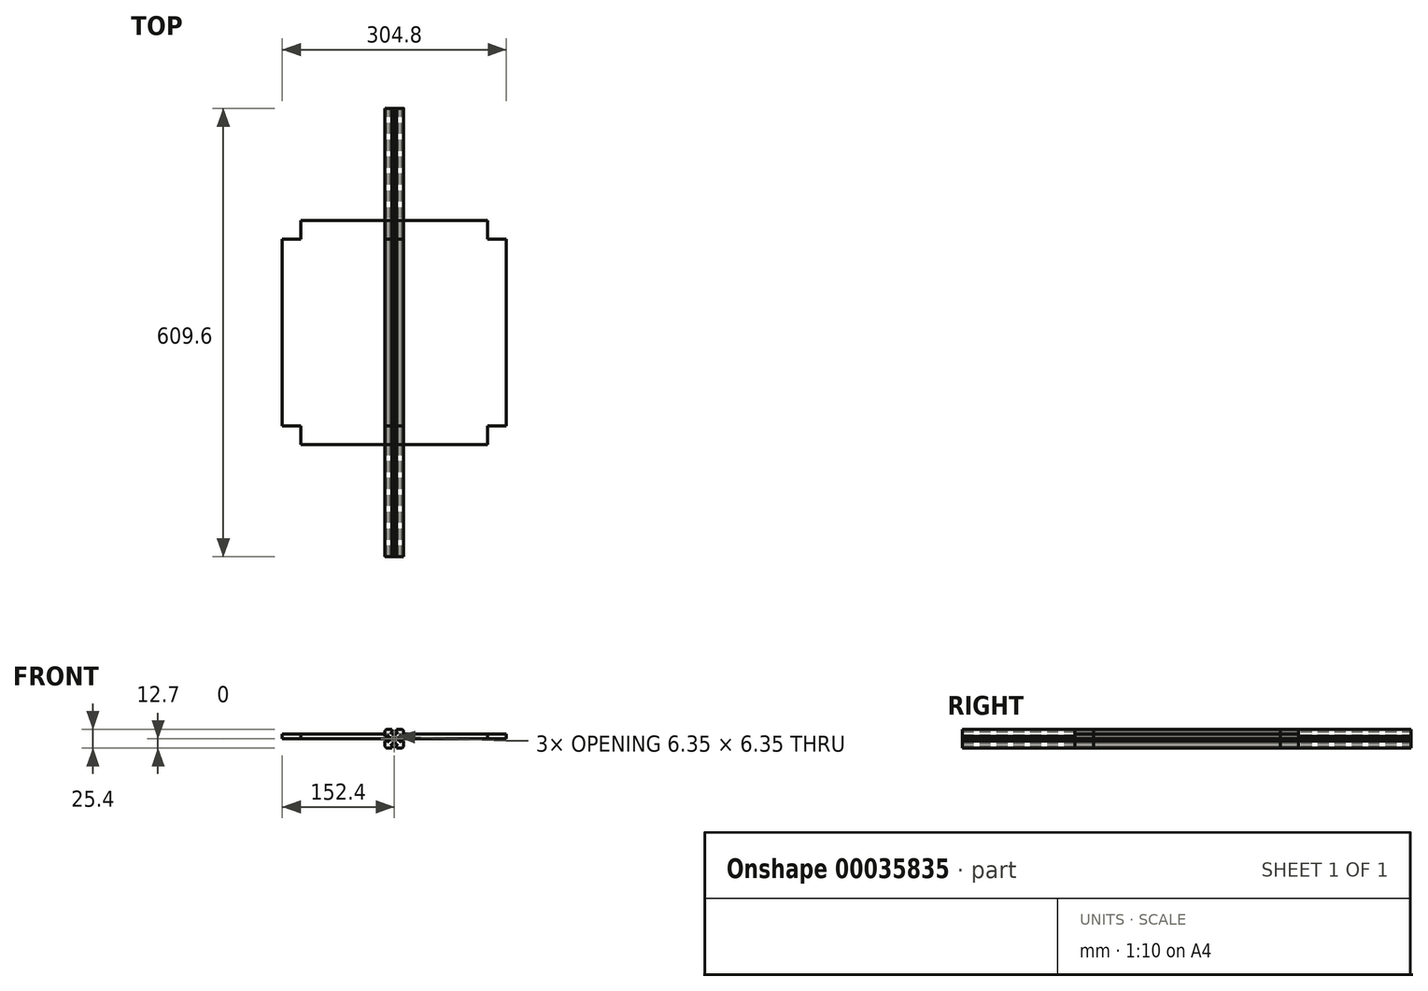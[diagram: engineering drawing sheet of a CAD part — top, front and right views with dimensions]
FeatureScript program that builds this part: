
annotation { "Feature Type Name" : "Feature", "Feature Type Description" : "" }
export const myFeature = defineFeature(function(context is Context, id is Id, definition is map)
    precondition{}
    {
        {
            var Q0;
            Q0=qCreatedBy(makeId("Front.planeOp"),FACE);
            var sketch = newSketch(context, id + "F0", { "sketchPlane" : qUnion([Q0])});
            skLineSegment(sketch, "E0", {"start": v(0, 12.7) * mm, "end": v(0, 0) * mm, "construction": true});
            skLineSegment(sketch, "E1", {"start": v(0, 0) * mm, "end": v(12.7, 0) * mm, "construction": true});
            skLineSegment(sketch, "E2", {"start": v(0, 0) * mm, "end": v(12.7, 12.7) * mm, "construction": true});
            skLineSegment(sketch, "E3", {"start": v(9.53, 12.7) * mm, "end": v(3.18, 12.7) * mm});
            skLineSegment(sketch, "E4", {"start": v(3.18, 12.7) * mm, "end": v(3.18, 9.53) * mm});
            skLineSegment(sketch, "E5", {"start": v(3.18, 9.53) * mm, "end": v(5.03, 9.53) * mm});
            skLineSegment(sketch, "E6", {"start": v(5.03, 9.53) * mm, "end": v(1.86, 6.35) * mm});
            skLineSegment(sketch, "E7", {"start": v(1.86, 6.35) * mm, "end": v(0, 6.35) * mm});
            skLineSegment(sketch, "E8.MirrorCS", {"start": v(6.35, 1.86) * mm, "end": v(6.35, 0) * mm});
            skLineSegment(sketch, "E9.MirrorCS", {"start": v(9.53, 5.03) * mm, "end": v(6.35, 1.86) * mm});
            skLineSegment(sketch, "E10.MirrorCS", {"start": v(9.53, 3.17) * mm, "end": v(9.53, 5.03) * mm});
            skLineSegment(sketch, "E11.MirrorCS", {"start": v(12.7, 9.53) * mm, "end": v(12.7, 3.17) * mm});
            skLineSegment(sketch, "E12.MirrorCS", {"start": v(12.7, 3.18) * mm, "end": v(9.53, 3.18) * mm});
            skPoint(sketch, "E13.visualSharp", {"position": v(12.7, 12.7) * mm});
            skArc(sketch, "E13.filletArc", {"start": v(12.7, 9.53) * mm, "mid": v(11.77, 11.77) * mm, "end": v(9.53, 12.7) * mm});
            skLineSegment(sketch, "E14.1.0", {"start": v(-6.35, 1.86) * mm, "end": v(-6.35, 0) * mm});
            skLineSegment(sketch, "E14.1.1", {"start": v(-9.52, 5.03) * mm, "end": v(-6.35, 1.86) * mm});
            skLineSegment(sketch, "E14.1.2", {"start": v(-9.53, 3.18) * mm, "end": v(-9.53, 5.03) * mm});
            skLineSegment(sketch, "E14.1.3", {"start": v(-12.7, 3.18) * mm, "end": v(-9.53, 3.18) * mm});
            skLineSegment(sketch, "E14.1.4", {"start": v(-12.7, 9.53) * mm, "end": v(-12.7, 3.18) * mm});
            skArc(sketch, "E14.1.5", {"start": v(-9.53, 12.7) * mm, "mid": v(-11.77, 11.77) * mm, "end": v(-12.7, 9.53) * mm});
            skLineSegment(sketch, "E14.1.6", {"start": v(-9.53, 12.7) * mm, "end": v(-3.17, 12.7) * mm});
            skLineSegment(sketch, "E14.1.7", {"start": v(-3.17, 12.7) * mm, "end": v(-3.17, 9.53) * mm});
            skLineSegment(sketch, "E14.1.8", {"start": v(-3.17, 9.53) * mm, "end": v(-5.03, 9.53) * mm});
            skLineSegment(sketch, "E14.1.9", {"start": v(-5.03, 9.53) * mm, "end": v(-1.86, 6.35) * mm});
            skLineSegment(sketch, "E14.1.10", {"start": v(-1.86, 6.35) * mm, "end": v(0, 6.35) * mm});
            skLineSegment(sketch, "E14.2.0", {"start": v(-1.86, -6.35) * mm, "end": v(0, -6.35) * mm});
            skLineSegment(sketch, "E14.2.1", {"start": v(-5.03, -9.53) * mm, "end": v(-1.86, -6.35) * mm});
            skLineSegment(sketch, "E14.2.2", {"start": v(-3.17, -9.53) * mm, "end": v(-5.03, -9.53) * mm});
            skLineSegment(sketch, "E14.2.3", {"start": v(-3.18, -12.7) * mm, "end": v(-3.18, -9.53) * mm});
            skLineSegment(sketch, "E14.2.4", {"start": v(-9.53, -12.7) * mm, "end": v(-3.18, -12.7) * mm});
            skArc(sketch, "E14.2.5", {"start": v(-12.7, -9.53) * mm, "mid": v(-11.77, -11.77) * mm, "end": v(-9.53, -12.7) * mm});
            skLineSegment(sketch, "E14.2.6", {"start": v(-12.7, -9.53) * mm, "end": v(-12.7, -3.17) * mm});
            skLineSegment(sketch, "E14.2.7", {"start": v(-12.7, -3.17) * mm, "end": v(-9.53, -3.17) * mm});
            skLineSegment(sketch, "E14.2.8", {"start": v(-9.52, -3.17) * mm, "end": v(-9.52, -5.03) * mm});
            skLineSegment(sketch, "E14.2.9", {"start": v(-9.53, -5.03) * mm, "end": v(-6.35, -1.86) * mm});
            skLineSegment(sketch, "E14.2.10", {"start": v(-6.35, -1.86) * mm, "end": v(-6.35, 0) * mm});
            skLineSegment(sketch, "E14.3.0", {"start": v(6.35, -1.86) * mm, "end": v(6.35, 0) * mm});
            skLineSegment(sketch, "E14.3.1", {"start": v(9.52, -5.03) * mm, "end": v(6.35, -1.86) * mm});
            skLineSegment(sketch, "E14.3.2", {"start": v(9.53, -3.18) * mm, "end": v(9.53, -5.03) * mm});
            skLineSegment(sketch, "E14.3.3", {"start": v(12.7, -3.18) * mm, "end": v(9.53, -3.18) * mm});
            skLineSegment(sketch, "E14.3.4", {"start": v(12.7, -9.53) * mm, "end": v(12.7, -3.18) * mm});
            skArc(sketch, "E14.3.5", {"start": v(9.53, -12.7) * mm, "mid": v(11.77, -11.77) * mm, "end": v(12.7, -9.53) * mm});
            skLineSegment(sketch, "E14.3.6", {"start": v(9.53, -12.7) * mm, "end": v(3.17, -12.7) * mm});
            skLineSegment(sketch, "E14.3.7", {"start": v(3.17, -12.7) * mm, "end": v(3.17, -9.53) * mm});
            skLineSegment(sketch, "E14.3.8", {"start": v(3.17, -9.53) * mm, "end": v(5.03, -9.53) * mm});
            skLineSegment(sketch, "E14.3.9", {"start": v(5.03, -9.53) * mm, "end": v(1.86, -6.35) * mm});
            skLineSegment(sketch, "E14.3.10", {"start": v(1.86, -6.35) * mm, "end": v(0, -6.35) * mm});
            skPoint(sketch, "E14.center", {"position": v(0, 0) * mm});
            skLineSegment(sketch, "E15", {"start": v(0, 3.18) * mm, "end": v(1.59, 3.18) * mm});
            skLineSegment(sketch, "E16.MirrorCS", {"start": v(3.18, 0) * mm, "end": v(3.18, 1.59) * mm});
            skPoint(sketch, "E17.visualSharp", {"position": v(3.18, 3.18) * mm});
            skArc(sketch, "E17.filletArc", {"start": v(3.18, 1.59) * mm, "mid": v(2.71, 2.71) * mm, "end": v(1.59, 3.18) * mm});
            skLineSegment(sketch, "E18.1.1", {"start": v(-3.18, 0) * mm, "end": v(-3.18, 1.59) * mm});
            skLineSegment(sketch, "E18.1.2", {"start": v(0, 3.18) * mm, "end": v(-1.59, 3.18) * mm});
            skArc(sketch, "E18.1.3", {"start": v(-1.59, 3.18) * mm, "mid": v(-2.71, 2.71) * mm, "end": v(-3.18, 1.59) * mm});
            skLineSegment(sketch, "E18.2.1", {"start": v(0, -3.18) * mm, "end": v(-1.59, -3.18) * mm});
            skLineSegment(sketch, "E18.2.2", {"start": v(-3.18, 0) * mm, "end": v(-3.18, -1.59) * mm});
            skArc(sketch, "E18.2.3", {"start": v(-3.18, -1.59) * mm, "mid": v(-2.71, -2.71) * mm, "end": v(-1.59, -3.18) * mm});
            skLineSegment(sketch, "E18.3.1", {"start": v(3.18, 0) * mm, "end": v(3.18, -1.59) * mm});
            skLineSegment(sketch, "E18.3.2", {"start": v(0, -3.18) * mm, "end": v(1.59, -3.18) * mm});
            skArc(sketch, "E18.3.3", {"start": v(1.59, -3.18) * mm, "mid": v(2.71, -2.71) * mm, "end": v(3.18, -1.59) * mm});
            skSolve(sketch);
        }
        {
            assignVariable(context, id + "F1", {"name" : "length", "anyValue" : 254 * mm});
        }
        {
            var Q0;
            Q0 = qSketchRegion(id + "F0", true);
            extrude(context, id + "F2", {"entities" : qUnion([Q0]), "endBound" : BoundingType.SYMMETRIC, "depth" : getVariable(context, 'length')});
        }
        {
            assignVariable(context, id + "F3", {"name" : "length2", "anyValue" : 609.6 * mm});
        }
        {
            var Q0;
            Q0 = qSketchRegion(id + "F0", true);
            extrude(context, id + "F4", {"entities" : qUnion([Q0]), "endBound" : BoundingType.SYMMETRIC, "depth" : getVariable(context, 'length2')});
        }
        {
            assignVariable(context, id + "F5", {"name" : "length3", "anyValue" : 304.8 * mm});
        }
        {
            var Q0;
            Q0 = qSketchRegion(id + "F0", true);
            extrude(context, id + "F6", {"entities" : qUnion([Q0]), "endBound" : BoundingType.SYMMETRIC, "depth" : getVariable(context, 'length3')});
        }
        {
            var Q0;
            Q0=qCreatedBy(makeId("Top.planeOp"),FACE);
            var sketch = newSketch(context, id + "F7", { "sketchPlane" : qUnion([Q0])});
            skLineSegment(sketch, "E19.rect.bottom", {"start": v(152.4, 152.4) * mm, "end": v(-152.4, 152.4) * mm});
            skLineSegment(sketch, "E19.rect.top", {"start": v(152.4, -152.4) * mm, "end": v(-152.4, -152.4) * mm});
            skLineSegment(sketch, "E19.rect.left", {"start": v(152.4, 152.4) * mm, "end": v(152.4, -152.4) * mm});
            skLineSegment(sketch, "E19.rect.right", {"start": v(-152.4, 152.4) * mm, "end": v(-152.4, -152.4) * mm});
            skPoint(sketch, "E19.rect.middle", {"position": v(0, 0) * mm});
            skLineSegment(sketch, "E20.bottom", {"start": v(152.4, 152.4) * mm, "end": v(127, 152.4) * mm, "construction": true});
            skLineSegment(sketch, "E20.top", {"start": v(152.4, 127) * mm, "end": v(127, 127) * mm});
            skLineSegment(sketch, "E20.left", {"start": v(152.4, 152.4) * mm, "end": v(152.4, 127) * mm, "construction": true});
            skLineSegment(sketch, "E20.right", {"start": v(127, 152.4) * mm, "end": v(127, 127) * mm});
            skLineSegment(sketch, "E21.1.1", {"start": v(-127, 152.4) * mm, "end": v(-127, 127) * mm});
            skLineSegment(sketch, "E21.1.2", {"start": v(-152.4, 127) * mm, "end": v(-127, 127) * mm});
            skLineSegment(sketch, "E21.2.1", {"start": v(-152.4, -127) * mm, "end": v(-127, -127) * mm});
            skLineSegment(sketch, "E21.2.2", {"start": v(-127, -152.4) * mm, "end": v(-127, -127) * mm});
            skLineSegment(sketch, "E21.3.1", {"start": v(127, -152.4) * mm, "end": v(127, -127) * mm});
            skLineSegment(sketch, "E21.3.2", {"start": v(152.4, -127) * mm, "end": v(127, -127) * mm});
            skSolve(sketch);
        }
        {
            var Q0;
            {var subQ5=sQuery(id+"F7.wireOp",EDGE,"E20.top");Q0=makeQuery(id+"F7.imprint","IMPRINT",FACE,{"disambiguationData":[TD([[makeQuery(id+"F7.imprint","IMPRINT",EDGE,{"derivedFrom":subQ5}),1.0]])]});}
            extrude(context, id + "F8", {"entities" : qUnion([Q0]), "depth" : 6.35 * mm});
        }
    });
